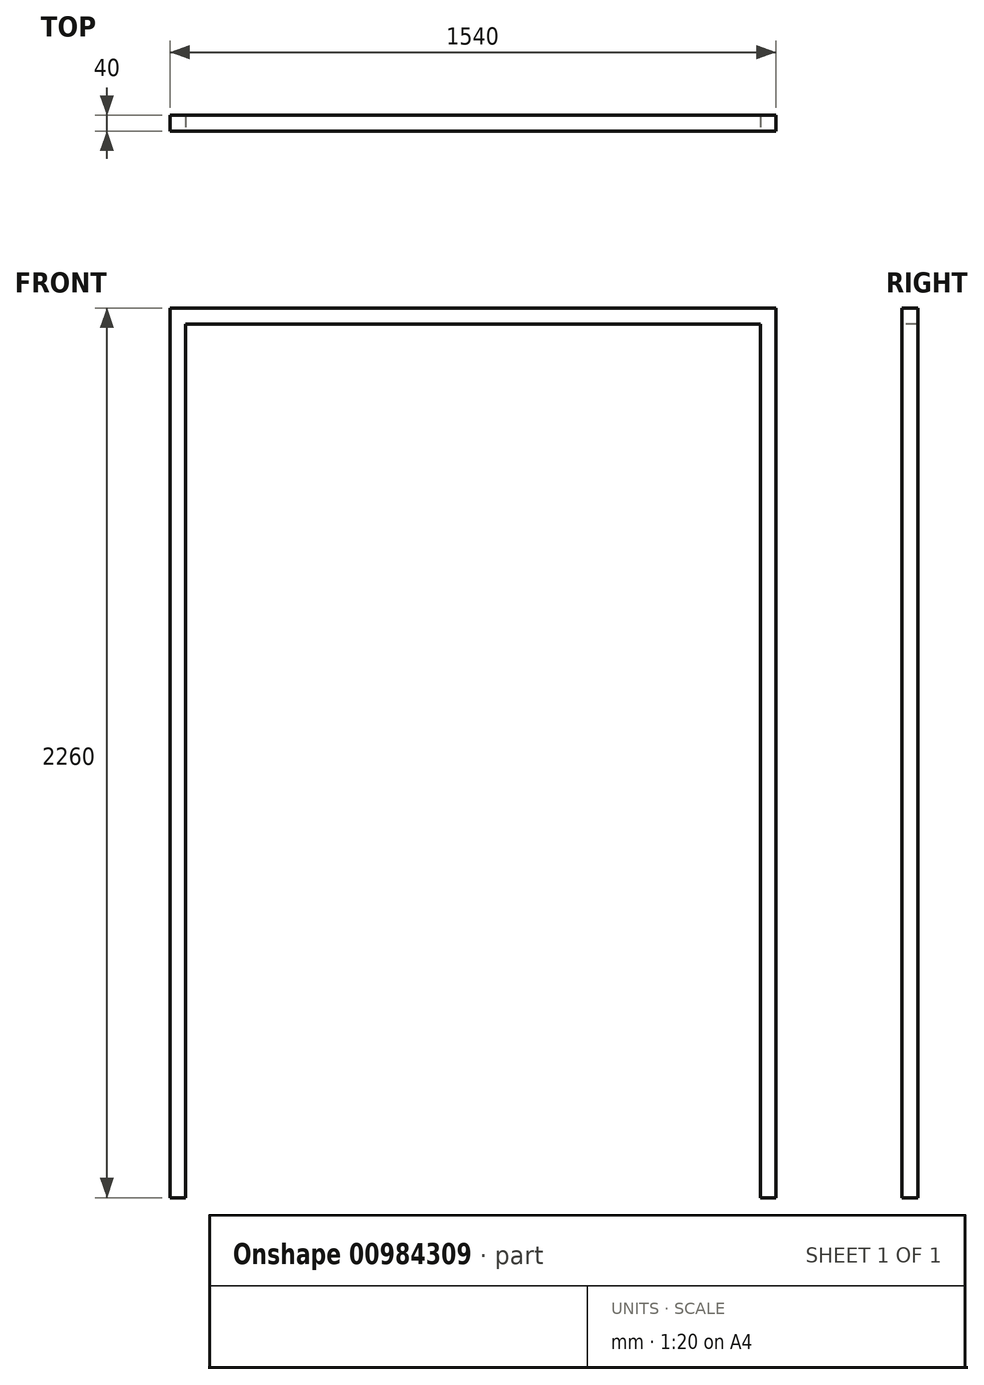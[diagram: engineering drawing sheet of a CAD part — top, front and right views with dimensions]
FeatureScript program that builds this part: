
annotation { "Feature Type Name" : "Feature", "Feature Type Description" : "" }
export const myFeature = defineFeature(function(context is Context, id is Id, definition is map)
    precondition{}
    {
        {
            var Q0;
            Q0=qCreatedBy(makeId("Top.planeOp"),FACE);
            var sketch = newSketch(context, id + "F0", { "sketchPlane" : qUnion([Q0])});
            skLineSegment(sketch, "E0.bottom", {"start": v(20, -20) * mm, "end": v(-20, -20) * mm});
            skLineSegment(sketch, "E0.top", {"start": v(20, 20) * mm, "end": v(-20, 20) * mm});
            skLineSegment(sketch, "E0.left", {"start": v(20, -20) * mm, "end": v(20, 20) * mm});
            skLineSegment(sketch, "E0.right", {"start": v(-20, -20) * mm, "end": v(-20, 20) * mm});
            skPoint(sketch, "E0.middle", {"position": v(0, 0) * mm});
            skSolve(sketch);
        }
        {
            var Q0;
            Q0=qCreatedBy(makeId("Front.planeOp"),FACE);
            var sketch = newSketch(context, id + "F1", { "sketchPlane" : qUnion([Q0])});
            skLineSegment(sketch, "E1", {"start": v(0, 0) * mm, "end": v(0, 2240) * mm});
            skLineSegment(sketch, "E2", {"start": v(0, 2240) * mm, "end": v(1500, 2240) * mm});
            skLineSegment(sketch, "E3", {"start": v(1500, 2240) * mm, "end": v(1500, 0) * mm});
            skSolve(sketch);
        }
        {
            var Q0;
            Q0=makeQuery(id+"F0.imprint","IMPRINT",FACE,{"disambiguationData":[TD([[makeQuery(id+"F0.imprint","IMPRINT",EDGE,{"derivedFrom":sQuery(id+"F0.wireOp",EDGE,"E0.bottom")}),-1.0]])]});
            var Q1;
            Q1=sQuery(id+"F1.wireOp",EDGE,"E1");
            var Q2;
            Q2=sQuery(id+"F1.wireOp",EDGE,"E2");
            var Q3;
            Q3=sQuery(id+"F1.wireOp",EDGE,"E3");
            sweep(context, id + "F2", {"profiles" : qUnion([Q0]), "path" : qUnion([Q1, Q2, Q3])});
        }
    });
